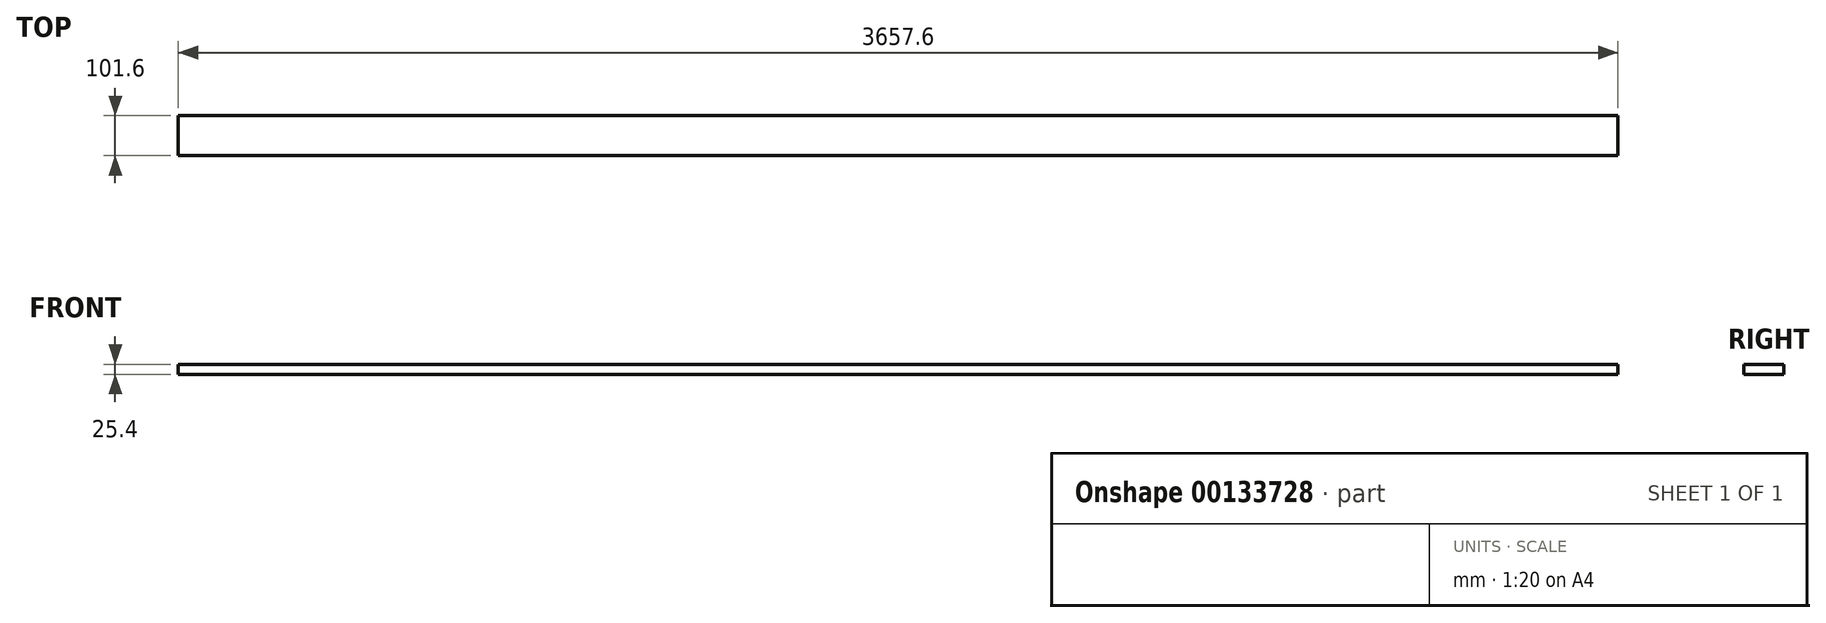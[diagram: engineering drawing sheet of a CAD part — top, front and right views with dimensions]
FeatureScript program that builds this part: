
annotation { "Feature Type Name" : "Feature", "Feature Type Description" : "" }
export const myFeature = defineFeature(function(context is Context, id is Id, definition is map)
    precondition{}
    {
        {
            var Q0;
            Q0=qCreatedBy(makeId("Top.planeOp"),FACE);
            var sketch = newSketch(context, id + "F0", { "sketchPlane" : qUnion([Q0])});
            skLineSegment(sketch, "E0.bottom", {"start": v(0, 0) * mm, "end": v(3657.6, 0) * mm});
            skLineSegment(sketch, "E0.top", {"start": v(0, 101.6) * mm, "end": v(3657.6, 101.6) * mm});
            skLineSegment(sketch, "E0.left", {"start": v(0, 0) * mm, "end": v(0, 101.6) * mm});
            skLineSegment(sketch, "E0.right", {"start": v(3657.6, 0) * mm, "end": v(3657.6, 101.6) * mm});
            skSolve(sketch);
        }
        {
            var Q0;
            Q0 = qSketchRegion(id + "F0", true);
            extrude(context, id + "F1", {"entities" : qUnion([Q0]), "depth" : 25.4 * mm});
        }
    });
